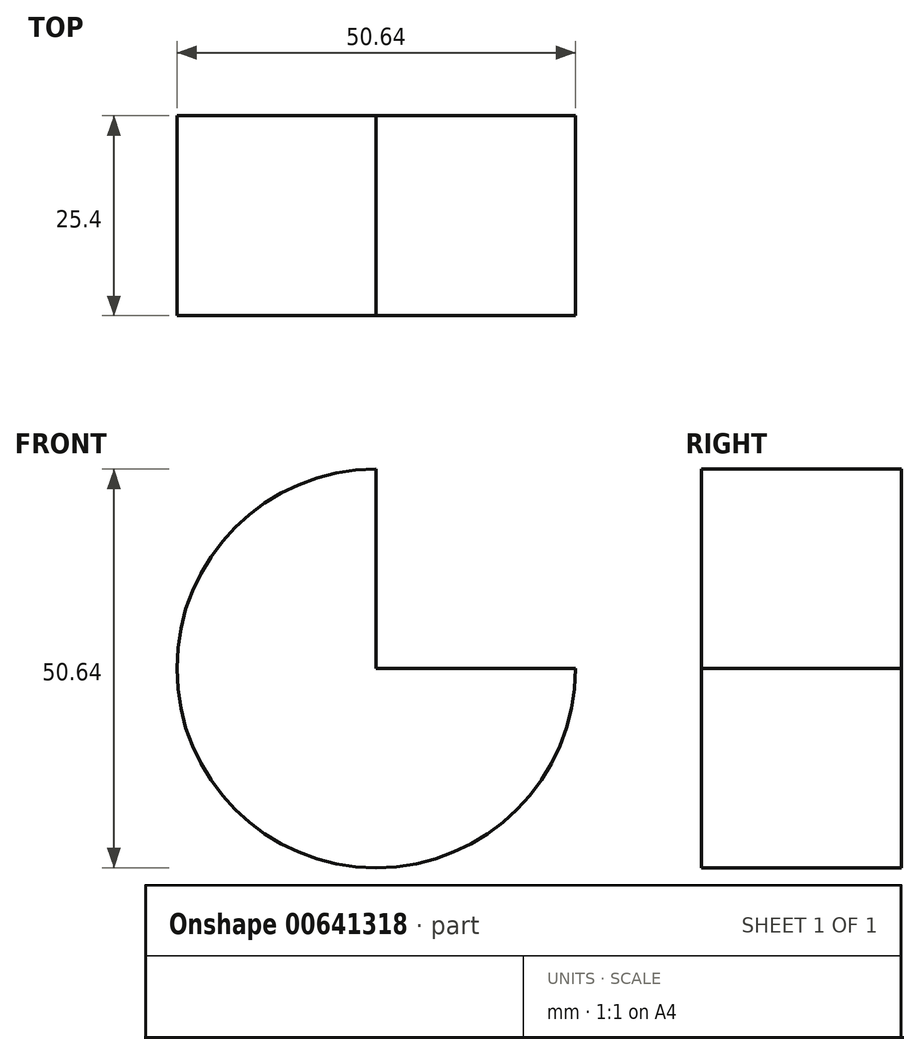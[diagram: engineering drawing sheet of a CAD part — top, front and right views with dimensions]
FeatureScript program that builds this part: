
annotation { "Feature Type Name" : "Feature", "Feature Type Description" : "" }
export const myFeature = defineFeature(function(context is Context, id is Id, definition is map)
    precondition{}
    {
        {
            var Q0;
            Q0=qCreatedBy(makeId("Front.planeOp"),FACE);
            var sketch = newSketch(context, id + "F0", { "sketchPlane" : qUnion([Q0])});
            skLineSegment(sketch, "E0", {"start": v(0, 0) * mm, "end": v(25.4, 0) * mm});
            skLineSegment(sketch, "E1", {"start": v(25.4, 0) * mm, "end": v(25.4, 50.8) * mm});
            skLineSegment(sketch, "E2", {"start": v(25.4, 50.8) * mm, "end": v(0, 50.8) * mm});
            skLineSegment(sketch, "E3", {"start": v(0, 50.8) * mm, "end": v(0, 0) * mm});
            skCircle(sketch, "E4", {"center": v(0, 0) * mm, "radius": 25.32 * mm});
            skSolve(sketch);
        }
        {
            var Q0;
            {var subQ0=sQuery(id+"F0.wireOp",EDGE,"E3");var subQ1=sQuery(id+"F0.wireOp",EDGE,"E0");var subQ2=makeQuery(id+"F0.imprint","INTERSECT",VERTEX,{"derivedFrom":[subQ1,subQ0]});Q0=makeQuery(id+"F0.imprint","IMPRINT",FACE,{"disambiguationData":[TD([[makeQuery(id+"F0.imprint","IMPRINT",EDGE,{"disambiguationData":[TD([[subQ2,-1.0]])],"derivedFrom":subQ1}),-1.0]])]});}
            extrude(context, id + "F1", {"entities" : qUnion([Q0]), "depth" : 25.4 * mm, "offsetDistance" : 25.4 * mm});
        }
    });
